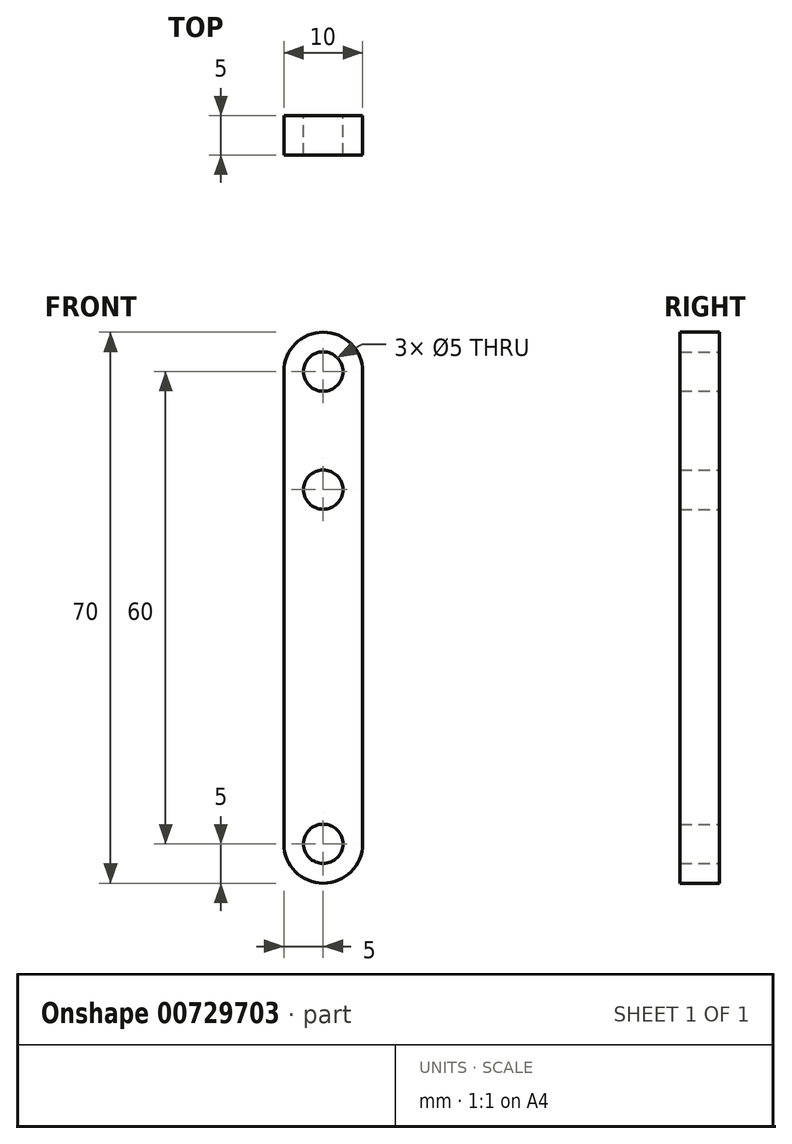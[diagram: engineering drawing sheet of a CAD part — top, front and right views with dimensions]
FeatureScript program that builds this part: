
annotation { "Feature Type Name" : "Feature", "Feature Type Description" : "" }
export const myFeature = defineFeature(function(context is Context, id is Id, definition is map)
    precondition{}
    {
        {
            var Q0;
            Q0=qCreatedBy(makeId("Front.planeOp"),FACE);
            var sketch = newSketch(context, id + "F0", { "sketchPlane" : qUnion([Q0])});
            skArc(sketch, "E0", {"start": v(5, 30) * mm, "mid": v(0, 35) * mm, "end": v(-5, 30) * mm});
            skArc(sketch, "E1", {"start": v(-5, -30) * mm, "mid": v(0, -35) * mm, "end": v(5, -30) * mm});
            skCircle(sketch, "E2", {"center": v(0, 15) * mm, "radius": 2.5 * mm});
            skLineSegment(sketch, "E3", {"start": v(-5, 30) * mm, "end": v(-5, -30) * mm});
            skLineSegment(sketch, "E4", {"start": v(5, 30) * mm, "end": v(5, -30) * mm});
            skCircle(sketch, "E5", {"center": v(0, 30) * mm, "radius": 2.5 * mm});
            skCircle(sketch, "E6", {"center": v(0, -30) * mm, "radius": 2.5 * mm});
            skSolve(sketch);
        }
        {
            var Q0;
            Q0=makeQuery(id+"F0.imprint","IMPRINT",FACE,{"disambiguationData":[TD([[makeQuery(id+"F0.imprint","IMPRINT",EDGE,{"derivedFrom":sQuery(id+"F0.wireOp",EDGE,"E0")}),1.0]])]});
            extrude(context, id + "F1", {"entities" : qUnion([Q0]), "endBound" : BoundingType.SYMMETRIC, "depth" : 5 * mm, "offsetDistance" : 25 * mm});
        }
    });
